# Revit family: Drain_Floor_Zurn-Z319-Thoroflush
name_source: partatom
category: Plumbing Fixtures
units: mm (PartAtom-declared; Revit-internal decimal feet)

## family parameters
Always vertical = Yes
Cut with Voids When Loaded = No
Maintain Annotation Orientation = No
OmniClass Number = 23.45.55.21
OmniClass Title = Drains (Wastes)
Part Type = Normal
Room Calculation Point = No
Round Connector Dimension = Use Radius
Shared = No
Work Plane-Based = No

## types (6) — shared parameters
Approx. Weight (Lbs) = 118 "
Assembly Code = D2030300
CW Connection = No
Default Elevation = 20 "
Description = LARGE CAPACITY THOROFLUSH DRAIN
Diameter = 24 "
Grate Material = Bronze - Zurn - Polished Nickel
Grate Open Area = 232 SF
HW Connection = No
Main Material = Iron - Zurn - Cast - White A.R.E Coated
Manufacturer = Zurn Water, LLC
Manufacurer Brand = Zurn
Model = ZN319
Modified Date = 12/19/25
Product Documentation Link = https://files.zurn.com
Product Page URL = https://www.zurn.com
Product data url = https://www.bimobject.com
URL = www.zurn.com
Vent Connection = No
Waste Connection = Yes
zero-valued in all types: CWFU, HWFU, WFU

## per-type parameters (varying)
| type | Body Height  ' E ' | Pipe Size 'A' (Inner Diameter) | Pipe Size 'A' (Inner Radius) | Pipe Size 'A' (Nominal Diameter) | Pipe Size 'A' (Nominal Radius) | Pipe Size 'A' (Outer Diameter) | Pipe Size 'A' (Outer Radius) |
| ZN319-8 Inch Threaded Outlet | 11 " | 7.981 " | 3.991 " | 8 " | 4 " | 8.625 " | 4.313 " |
| ZN319-6 Inch Threaded Outlet | 11 " | 6.065 " | 3.033 " | 6 " | 3 " | 6.625 " | 3.313 " |
| ZN319-4 Inch Threaded Outlet | 11 " | 4.026 " | 2.013 " | 4 " | 2 " | 4.5 " | 2.25 " |
| ZN319-3 Inch Threaded Outlet | 11 " | 3.068 " | 1.534 " | 3 " | 1.5 " | 3.5 " | 1.75 " |
| ZN319-3 Inch Inside Caulk Outlet | 12.125 " | 3.068 " | 1.534 " | 3 " | 1.5 " | 3.5 " | 1.75 " |
| ZN319-4 Inch Inside Caulk Outlet | 12.125 " | 4.026 " | 2.013 " | 4 " | 2 " | 4.5 " | 2.25 " |

## geometry (parser evidence)
native form markers: Blend x6, Sweep x4
no freeform markers — native parametric forms only
